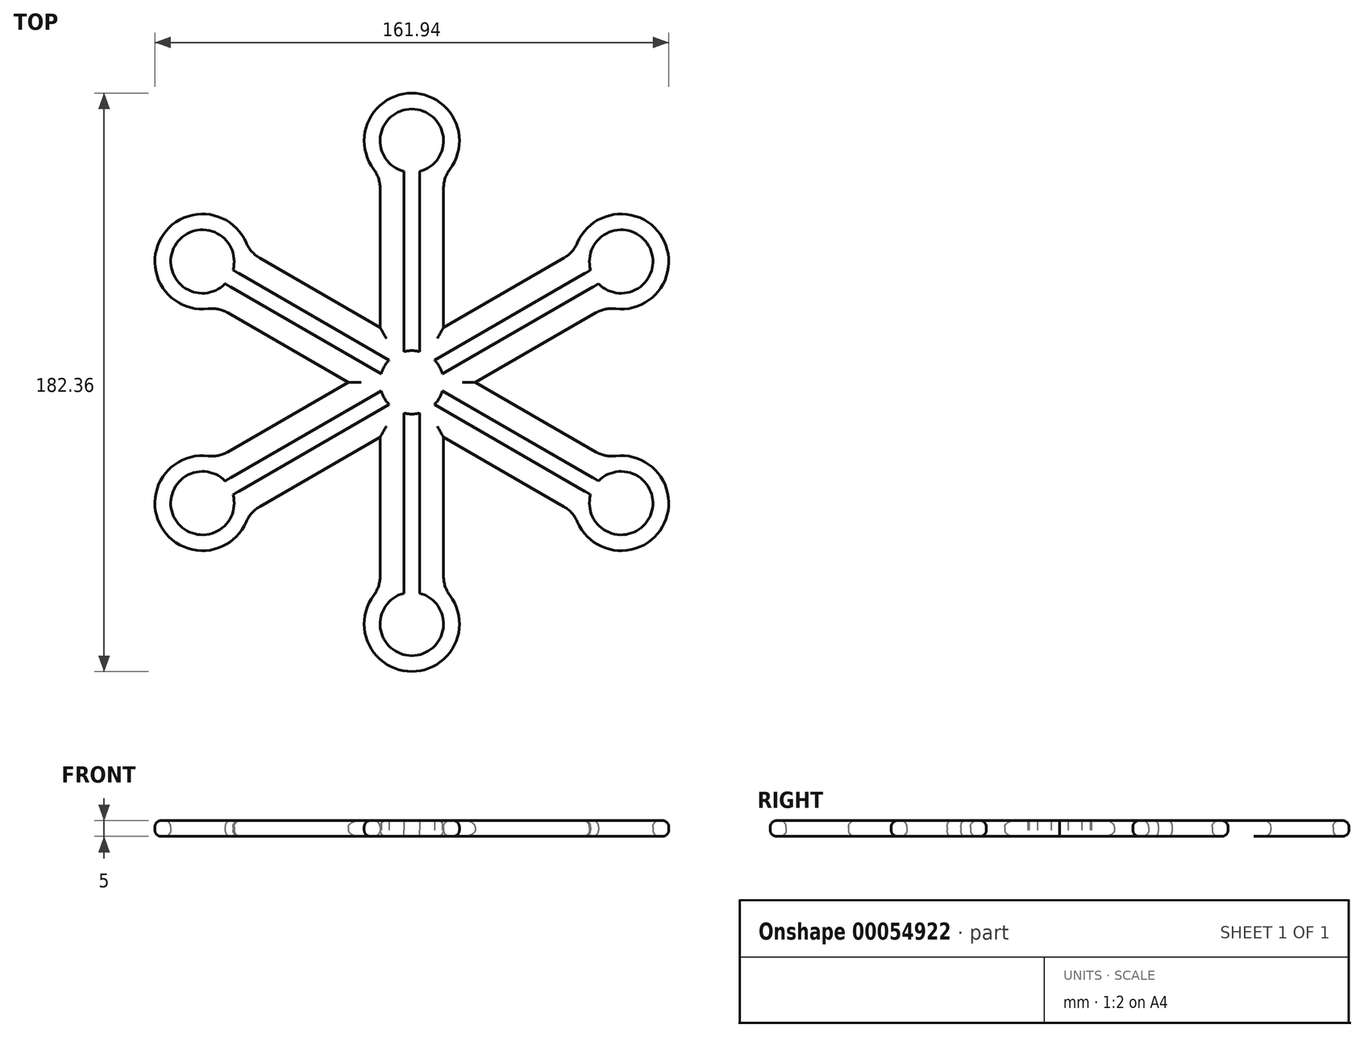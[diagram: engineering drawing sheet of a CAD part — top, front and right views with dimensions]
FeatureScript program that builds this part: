
annotation { "Feature Type Name" : "Feature", "Feature Type Description" : "" }
export const myFeature = defineFeature(function(context is Context, id is Id, definition is map)
    precondition{}
    {
        {
            var Q0;
            Q0=qCreatedBy(makeId("Top.planeOp"),FACE);
            var sketch = newSketch(context, id + "F0", { "sketchPlane" : qUnion([Q0])});
            skLineSegment(sketch, "E0", {"start": v(0, 0) * mm, "end": v(-10, 17.32) * mm});
            skLineSegment(sketch, "E1", {"start": v(0, 0) * mm, "end": v(0, 17.32) * mm, "construction": true});
            skLineSegment(sketch, "E2", {"start": v(0, 0) * mm, "end": v(10, 17.32) * mm});
            skLineSegment(sketch, "E3", {"start": v(-10, 17.32) * mm, "end": v(-10, 65) * mm});
            skLineSegment(sketch, "E4", {"start": v(10, 17.32) * mm, "end": v(10, 65) * mm});
            skCircle(sketch, "E5", {"center": v(0, 76.18) * mm, "radius": 15 * mm});
            skCircle(sketch, "E6", {"center": v(0, 76.18) * mm, "radius": 10 * mm});
            skSolve(sketch);
        }
        {
            var Q0;
            Q0=makeQuery(id+"F0.imprint","IMPRINT",FACE,{"disambiguationData":[TD([[makeQuery(id+"F0.imprint","IMPRINT",EDGE,{"derivedFrom":sQuery(id+"F0.wireOp",EDGE,"E0")}),-1.0]])]});
            var Q1;
            Q1=makeQuery(id+"F0.imprint","IMPRINT",FACE,{"disambiguationData":[TD([[makeQuery(id+"F0.imprint","IMPRINT",EDGE,{"derivedFrom":sQuery(id+"F0.wireOp",EDGE,"E6")}),-1.0]])]});
            extrude(context, id + "F1", {"entities" : qUnion([Q0, Q1]), "depth" : 5 * mm});
        }
        {
            var Q0;
            Q0=makeQuery(id+"F1.opExtrude","SWEPT_EDGE",EDGE,{"disambiguationData":[OSD([sQuery(id+"F0.wireOp",EDGE,"E3"),sQuery(id+"F0.wireOp",EDGE,"E5")])]});
            var Q1;
            Q1=makeQuery(id+"F1.opExtrude","SWEPT_EDGE",EDGE,{"disambiguationData":[OSD([sQuery(id+"F0.wireOp",EDGE,"E4"),sQuery(id+"F0.wireOp",EDGE,"E5")])]});
            fillet(context, id + "F2", {"entities" : qUnion([Q0, Q1]), "radius" : 10 * mm, "tangentPropagation" : true, "allowEdgeOverflow" : false});
        }
        {
            var Q0;
            Q0=makeQuery(id+"F1.opExtrude","SWEPT_BODY",BODY,{"disambiguationData":[OSD([sQuery(id+"F0.wireOp",EDGE,"E0"),sQuery(id+"F0.wireOp",EDGE,"E2"),sQuery(id+"F0.wireOp",EDGE,"E3"),sQuery(id+"F0.wireOp",EDGE,"E4"),sQuery(id+"F0.wireOp",EDGE,"E5"),sQuery(id+"F0.wireOp",EDGE,"E6")])]});
            var Q1;
            Q1=makeQuery(id+"F1.opExtrude","SWEPT_EDGE",EDGE,{"disambiguationData":[OSD([sQuery(id+"F0.wireOp",EDGE,"E0"),sQuery(id+"F0.wireOp",EDGE,"E2")])]});
            circularPattern(context, id + "F3", {"operationType" : NewBodyOperationType.ADD, "entities" : qUnion([Q0]), "axis" : qUnion([Q1]), "angle" : 60 * degree, "instanceCount" : 6});
        }
        {
            var Q0;
            Q0=qCreatedBy(makeId("Top.planeOp"),FACE);
            var sketch = newSketch(context, id + "F4", { "sketchPlane" : qUnion([Q0])});
            skLineSegment(sketch, "E7.0.0", {"start": v(-10, 61.18) * mm, "end": v(-10, 17.32) * mm});
            skLineSegment(sketch, "E7.0.1", {"start": v(-10, 17.32) * mm, "end": v(-47.98, 39.25) * mm});
            skArc(sketch, "E7.0.2", {"start": v(-47.98, 39.25) * mm, "mid": v(-50.47, 41.28) * mm, "end": v(-52.18, 43.98) * mm});
            skArc(sketch, "E7.0.3", {"start": v(-52.18, 43.98) * mm, "mid": v(-78.96, 45.6) * mm, "end": v(-64.18, 23.2) * mm});
            skArc(sketch, "E7.0.4", {"start": v(-64.18, 23.2) * mm, "mid": v(-60.98, 23.07) * mm, "end": v(-57.98, 21.93) * mm});
            skLineSegment(sketch, "E7.0.5", {"start": v(-57.98, 21.93) * mm, "end": v(-20, 0) * mm});
            skLineSegment(sketch, "E7.0.6", {"start": v(-20, 0) * mm, "end": v(-57.98, -21.93) * mm});
            skArc(sketch, "E7.0.7", {"start": v(-57.98, -21.93) * mm, "mid": v(-60.98, -23.07) * mm, "end": v(-64.18, -23.2) * mm});
            skArc(sketch, "E7.0.8", {"start": v(-64.18, -23.2) * mm, "mid": v(-78.96, -45.6) * mm, "end": v(-52.18, -43.98) * mm});
            skArc(sketch, "E7.0.9", {"start": v(-52.18, -43.98) * mm, "mid": v(-50.47, -41.28) * mm, "end": v(-47.98, -39.25) * mm});
            skLineSegment(sketch, "E7.0.10", {"start": v(-47.98, -39.25) * mm, "end": v(-10, -17.32) * mm});
            skLineSegment(sketch, "E7.0.11", {"start": v(-10, -17.32) * mm, "end": v(-10, -61.18) * mm});
            skArc(sketch, "E7.0.12", {"start": v(-10, -61.18) * mm, "mid": v(-10.51, -64.34) * mm, "end": v(-12, -67.18) * mm});
            skArc(sketch, "E7.0.13", {"start": v(-12, -67.18) * mm, "mid": v(0, -91.18) * mm, "end": v(12, -67.18) * mm});
            skArc(sketch, "E7.0.14", {"start": v(12, -67.18) * mm, "mid": v(10.51, -64.34) * mm, "end": v(10, -61.18) * mm});
            skLineSegment(sketch, "E7.0.15", {"start": v(10, -61.18) * mm, "end": v(10, -17.32) * mm});
            skLineSegment(sketch, "E7.0.16", {"start": v(10, -17.32) * mm, "end": v(47.98, -39.25) * mm});
            skArc(sketch, "E7.0.17", {"start": v(47.98, -39.25) * mm, "mid": v(50.47, -41.28) * mm, "end": v(52.18, -43.98) * mm});
            skArc(sketch, "E7.0.18", {"start": v(52.18, -43.98) * mm, "mid": v(78.96, -45.6) * mm, "end": v(64.18, -23.2) * mm});
            skArc(sketch, "E7.0.19", {"start": v(64.18, -23.2) * mm, "mid": v(60.98, -23.07) * mm, "end": v(57.98, -21.93) * mm});
            skLineSegment(sketch, "E7.0.20", {"start": v(57.98, -21.93) * mm, "end": v(20, 0) * mm});
            skLineSegment(sketch, "E7.0.21", {"start": v(20, 0) * mm, "end": v(57.98, 21.93) * mm});
            skArc(sketch, "E7.0.22", {"start": v(57.98, 21.93) * mm, "mid": v(60.98, 23.07) * mm, "end": v(64.18, 23.2) * mm});
            skArc(sketch, "E7.0.23", {"start": v(64.18, 23.2) * mm, "mid": v(78.96, 45.6) * mm, "end": v(52.18, 43.98) * mm});
            skArc(sketch, "E7.0.24", {"start": v(52.18, 43.98) * mm, "mid": v(50.47, 41.28) * mm, "end": v(47.98, 39.25) * mm});
            skLineSegment(sketch, "E7.0.25", {"start": v(47.98, 39.25) * mm, "end": v(10, 17.32) * mm});
            skLineSegment(sketch, "E7.0.26", {"start": v(10, 17.32) * mm, "end": v(10, 61.18) * mm});
            skArc(sketch, "E7.0.27", {"start": v(10, 61.18) * mm, "mid": v(10.51, 64.34) * mm, "end": v(12, 67.18) * mm});
            skArc(sketch, "E7.0.28", {"start": v(12, 67.18) * mm, "mid": v(0, 91.18) * mm, "end": v(-12, 67.18) * mm});
            skArc(sketch, "E7.0.29", {"start": v(-12, 67.18) * mm, "mid": v(-10.51, 64.34) * mm, "end": v(-10, 61.18) * mm});
            skCircle(sketch, "E8", {"center": v(0, 0) * mm, "radius": 10 * mm});
            skCircle(sketch, "E9.0", {"center": v(0, 76.18) * mm, "radius": 10 * mm});
            skCircle(sketch, "E10.0", {"center": v(-65.97, 38.1) * mm, "radius": 10 * mm});
            skCircle(sketch, "E11.0", {"center": v(-65.97, -38.1) * mm, "radius": 10 * mm});
            skCircle(sketch, "E12.0", {"center": v(0, -76.18) * mm, "radius": 10 * mm});
            skCircle(sketch, "E13.0", {"center": v(65.97, -38.1) * mm, "radius": 10 * mm});
            skCircle(sketch, "E14.0", {"center": v(65.97, 38.1) * mm, "radius": 10 * mm});
            skLineSegment(sketch, "E15", {"start": v(-2.5, 66.5) * mm, "end": v(-2.5, 9.68) * mm});
            skLineSegment(sketch, "E16", {"start": v(2.5, 66.5) * mm, "end": v(2.5, 9.68) * mm});
            skLineSegment(sketch, "E17", {"start": v(0, 76.18) * mm, "end": v(0, 0) * mm, "construction": true});
            skLineSegment(sketch, "E18", {"start": v(0, 0) * mm, "end": v(-65.97, 38.1) * mm, "construction": true});
            skLineSegment(sketch, "E19", {"start": v(0, 0) * mm, "end": v(-65.97, -38.1) * mm, "construction": true});
            skLineSegment(sketch, "E20", {"start": v(0, 0) * mm, "end": v(0, -76.18) * mm, "construction": true});
            skLineSegment(sketch, "E21", {"start": v(0, 0) * mm, "end": v(65.97, -38.1) * mm, "construction": true});
            skLineSegment(sketch, "E22", {"start": v(0, 0) * mm, "end": v(65.97, 38.1) * mm, "construction": true});
            skLineSegment(sketch, "E23", {"start": v(-56.34, 35.41) * mm, "end": v(-7.14, 7) * mm});
            skLineSegment(sketch, "E24", {"start": v(-58.84, 31.08) * mm, "end": v(-9.64, 2.68) * mm});
            skLineSegment(sketch, "E25", {"start": v(-9.64, -2.68) * mm, "end": v(-58.84, -31.08) * mm});
            skLineSegment(sketch, "E26", {"start": v(-7.14, -7) * mm, "end": v(-56.34, -35.41) * mm});
            skLineSegment(sketch, "E27", {"start": v(-2.5, -9.68) * mm, "end": v(-2.5, -66.5) * mm});
            skLineSegment(sketch, "E28", {"start": v(2.5, -9.68) * mm, "end": v(2.5, -66.5) * mm});
            skLineSegment(sketch, "E29", {"start": v(7.14, -7) * mm, "end": v(56.34, -35.41) * mm});
            skLineSegment(sketch, "E30", {"start": v(9.64, -2.68) * mm, "end": v(58.84, -31.08) * mm});
            skLineSegment(sketch, "E31", {"start": v(9.64, 2.68) * mm, "end": v(58.84, 31.08) * mm});
            skLineSegment(sketch, "E32", {"start": v(7.14, 7) * mm, "end": v(56.34, 35.41) * mm});
            skSolve(sketch);
        }
        {
            var Q0;
            {var subQ0=makeQuery(id+"F1.opExtrude","CAP_FACE",FACE,{"disambiguationData":[OSD([sQuery(id+"F0.wireOp",EDGE,"E0"),sQuery(id+"F0.wireOp",EDGE,"E2"),sQuery(id+"F0.wireOp",EDGE,"E3"),sQuery(id+"F0.wireOp",EDGE,"E4"),sQuery(id+"F0.wireOp",EDGE,"E5"),sQuery(id+"F0.wireOp",EDGE,"E6")])],"isStart":false});Q0=makeQuery(id+"F3.boolean.opBoolean","MERGE",FACE,{"derivedFrom":[subQ0,makeQuery(id+"F3.opPattern","COPY",FACE,{"derivedFrom":subQ0,"instanceName":"1"}),makeQuery(id+"F3.opPattern","COPY",FACE,{"derivedFrom":subQ0,"instanceName":"2"}),makeQuery(id+"F3.opPattern","COPY",FACE,{"derivedFrom":subQ0,"instanceName":"3"}),makeQuery(id+"F3.opPattern","COPY",FACE,{"derivedFrom":subQ0,"instanceName":"4"}),makeQuery(id+"F3.opPattern","COPY",FACE,{"derivedFrom":subQ0,"instanceName":"5"})]});}
            var Q1;
            {var subQ0=makeQuery(id+"F1.opExtrude","CAP_FACE",FACE,{"disambiguationData":[OSD([sQuery(id+"F0.wireOp",EDGE,"E0"),sQuery(id+"F0.wireOp",EDGE,"E2"),sQuery(id+"F0.wireOp",EDGE,"E3"),sQuery(id+"F0.wireOp",EDGE,"E4"),sQuery(id+"F0.wireOp",EDGE,"E5"),sQuery(id+"F0.wireOp",EDGE,"E6")])],"isStart":true});Q1=makeQuery(id+"F3.boolean.opBoolean","MERGE",FACE,{"derivedFrom":[subQ0,makeQuery(id+"F3.opPattern","COPY",FACE,{"derivedFrom":subQ0,"instanceName":"1"}),makeQuery(id+"F3.opPattern","COPY",FACE,{"derivedFrom":subQ0,"instanceName":"2"}),makeQuery(id+"F3.opPattern","COPY",FACE,{"derivedFrom":subQ0,"instanceName":"3"}),makeQuery(id+"F3.opPattern","COPY",FACE,{"derivedFrom":subQ0,"instanceName":"4"}),makeQuery(id+"F3.opPattern","COPY",FACE,{"derivedFrom":subQ0,"instanceName":"5"})]});}
            fillet(context, id + "F5", {"entities" : qUnion([Q0, Q1]), "radius" : 2 * mm, "tangentPropagation" : true, "allowEdgeOverflow" : false});
        }
        {
            var Q0;
            Q0 = qSketchRegion(id + "F4", true);
            var Q1;
            {var subQ0=sQuery(id+"F4.wireOp",EDGE,"E8");var subQ11=makeQuery(id+"F4.imprint","INTERSECT",VERTEX,{"derivedFrom":[subQ0,sQuery(id+"F4.wireOp",EDGE,"E31")]});Q1=makeQuery(id+"F4.imprint","IMPRINT",FACE,{"disambiguationData":[TD([[makeQuery(id+"F4.imprint","IMPRINT",EDGE,{"disambiguationData":[TD([[subQ11,-1.0]])],"derivedFrom":subQ0}),1.0]])]});}
            extrude(context, id + "F6", {"entities" : qUnion([Q0, Q1]), "operationType" : NewBodyOperationType.INTERSECT, "depth" : 25 * mm});
        }
    });
